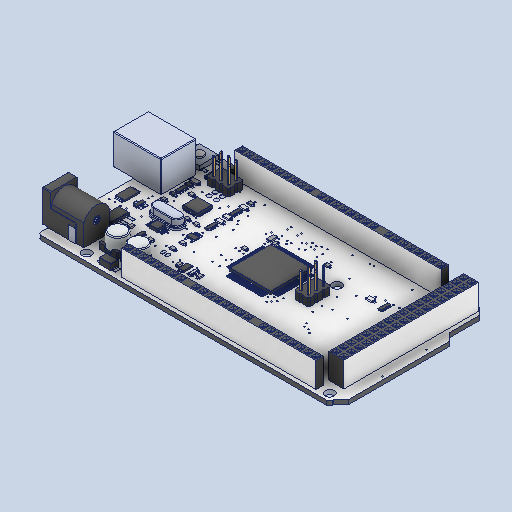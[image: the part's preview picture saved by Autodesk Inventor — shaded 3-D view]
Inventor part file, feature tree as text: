
AUTODESK INVENTOR PART (.ipt)
format: ipt  version: 2023 (Build 270158030, 158C)  size: 4,199,936 bytes
history: native  units: mm
features: other x1, fillet x1
ambient origin geometry x8: Origin, YZ Plane, XZ Plane, XY Plane, X Axis, Y Axis, Z Axis, Center Point
bodies: Solid1 (feature_tree)
feature tree (2):
  other  "arduinoMegaDetailed.STEP"
  fillet  "Fillet13"  [1 undecoded]
note: 1 required parameter value undecoded (feature->parameter linkage not recoverable at this tier; creation-order binding heuristic only, values carry confidence <= 0.55)
